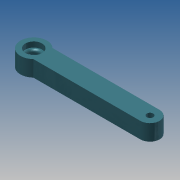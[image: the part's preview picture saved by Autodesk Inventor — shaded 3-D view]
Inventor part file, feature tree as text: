
AUTODESK INVENTOR PART (.ipt)
format: ipt  version: 2013 (Build 170138000, 138)  size: 129,536 bytes
history: native  units: mm
features: extrude x5, sketch x5, fillet x2
ambient origin geometry x8: Origin, YZ Plane, XZ Plane, XY Plane, X Axis, Y Axis, Z Axis, Center Point
bodies: Solid1 (feature_tree)
feature tree (12):
  extrude  "Extrusion1"  Depth=12.6mm
  extrude  "Extrusion2"  Depth=8.5mm
  extrude  "Extrusion5"  Depth=22.0mm
  extrude  "Extrusion6"  Depth=35.0mm
  extrude  "Extrusion7"  Depth=7.0mm TaperAngle=0.0deg
  fillet  "Fillet1"  Radius=13.0mm
  fillet  "Fillet2"  Radius=8.0mm
  sketch  "Sketch1"  dims[d0=153.0mm d2=12.6mm]
  sketch  "Sketch2"  dims[d3=15.0mm d4=8.5mm]
  sketch  "Sketch6"  dims[d5=21.1mm d6=0.0mm d7=22.0mm]
  sketch  "Sketch7"  dims[d9=7.0mm d10=0.0mm d25=35.0mm]
  sketch  "Sketch8"  dims[d27=10.0mm d28=0.0mm d29=7.0mm d30=0.0mm d31=13.0mm d32=8.0mm d33=0.0mm d34=3.5mm d35=3.5mm]
